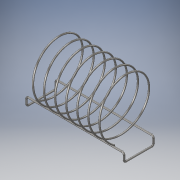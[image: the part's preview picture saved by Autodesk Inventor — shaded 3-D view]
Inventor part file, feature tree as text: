
AUTODESK INVENTOR PART (.ipt)
format: ipt  version: 2018 (Build 220112000, 112)  size: 618,496 bytes
history: native  units: mm
features: sketch x4, plane x4, sweep x1, helix x1
ambient origin geometry x8: Origin, YZ Plane, XZ Plane, XY Plane, X Axis, Y Axis, Z Axis, Center Point
bodies: Solid1 (feature_tree)
feature tree (10):
  sketch  "3D Sketch1"
  plane  "Work Plane1"
  sweep  "Sweep1"
  plane  "Work Plane3"
  sketch  "Sketch6"  dims[d3=15.0mm]
  plane  "Work Plane7"
  helix  "Coil1"  [1 undecoded]
  sketch  "Sketch4"  dims[d0=53.0mm d1=15.0mm d2=176.0mm]
  plane  "Work Plane6"
  sketch  "Sketch8"  dims[d4=53.0mm d5=15.0mm d6=176.0mm d10=3.0mm d11=3.0mm d12=3.0mm d13=3.0mm d14=3.0mm d15=3.0mm d16=3.0mm d17=3.0mm d18=3.0mm d19=0.0mm d20=0.0mm d27=18.0mm d28=6.0mm d29=3.0mm d33=60.0mm d34=176.0mm d35=7.0mm d36=140.0mm d37=70.0mm d38=0.0mm d39=90.0deg d40=90.0deg d41=0.0mm d42=0.0mm]
note: 1 required parameter value undecoded (feature->parameter linkage not recoverable at this tier; creation-order binding heuristic only, values carry confidence <= 0.55)
